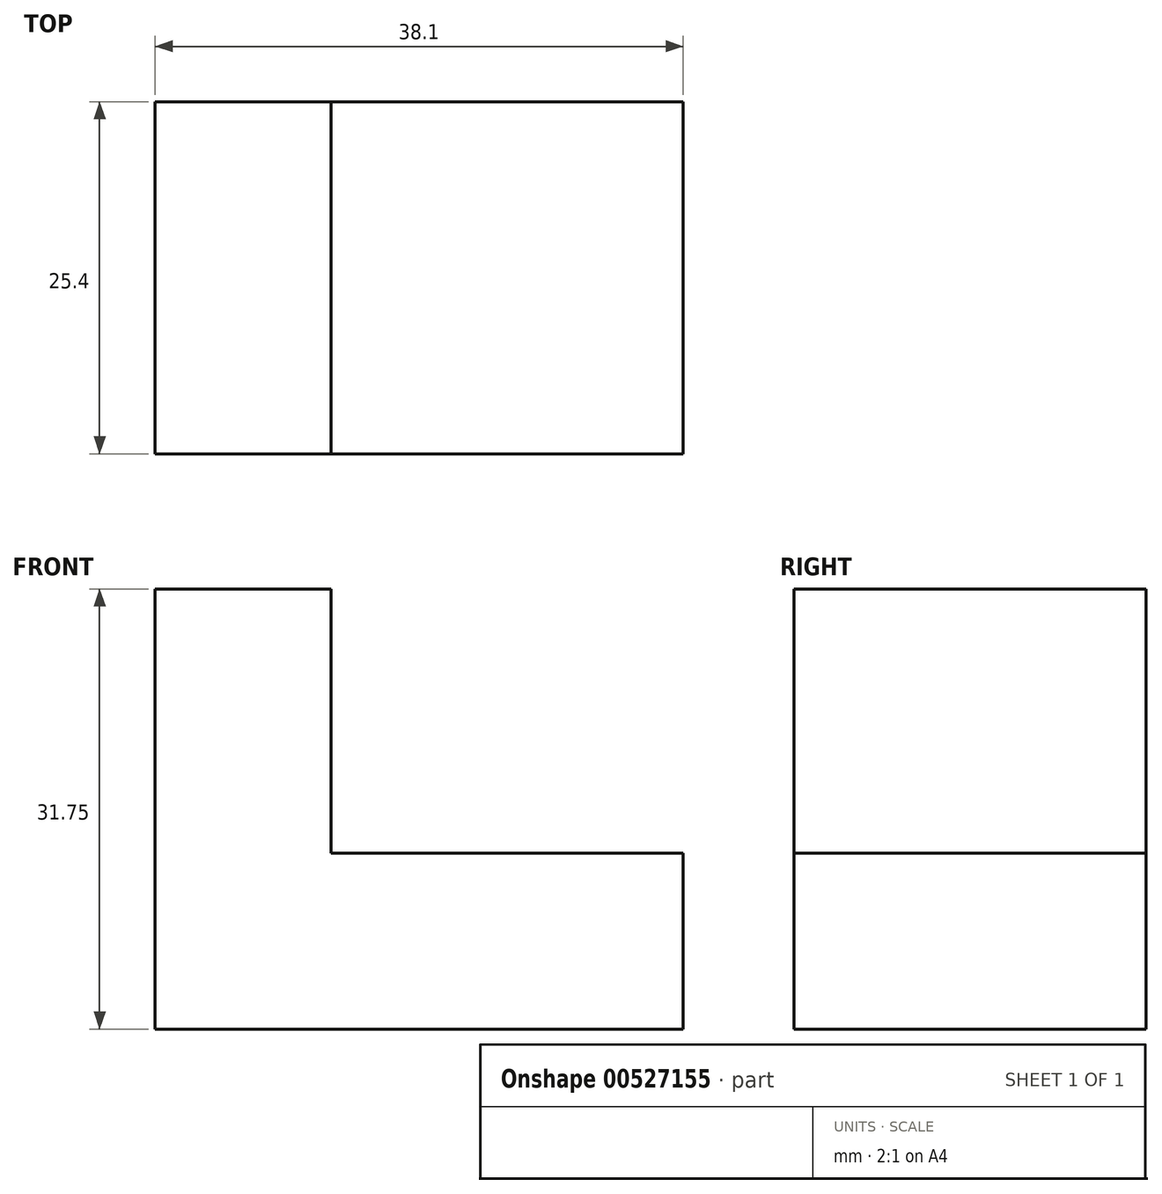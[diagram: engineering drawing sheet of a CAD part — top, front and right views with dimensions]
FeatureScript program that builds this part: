
annotation { "Feature Type Name" : "Feature", "Feature Type Description" : "" }
export const myFeature = defineFeature(function(context is Context, id is Id, definition is map)
    precondition{}
    {
        {
            var Q0;
            Q0=qCreatedBy(makeId("Front.planeOp"),FACE);
            var sketch = newSketch(context, id + "F0", { "sketchPlane" : qUnion([Q0])});
            skLineSegment(sketch, "E0", {"start": v(-68.63, 31.75) * mm, "end": v(-68.63, 0) * mm});
            skLineSegment(sketch, "E1", {"start": v(-68.63, 0) * mm, "end": v(-30.53, 0) * mm});
            skLineSegment(sketch, "E2", {"start": v(-30.53, 0) * mm, "end": v(-30.53, 12.7) * mm});
            skLineSegment(sketch, "E3", {"start": v(-30.53, 12.7) * mm, "end": v(-55.93, 12.7) * mm});
            skLineSegment(sketch, "E4", {"start": v(-55.93, 12.7) * mm, "end": v(-55.93, 31.75) * mm});
            skLineSegment(sketch, "E5", {"start": v(-68.63, 31.75) * mm, "end": v(-55.93, 31.75) * mm});
            skSolve(sketch);
        }
        {
            var Q0;
            Q0 = qSketchRegion(id + "F0", true);
            extrude(context, id + "F1", {"entities" : qUnion([Q0]), "depth" : 25.4 * mm, "offsetDistance" : 25.4 * mm});
        }
    });
